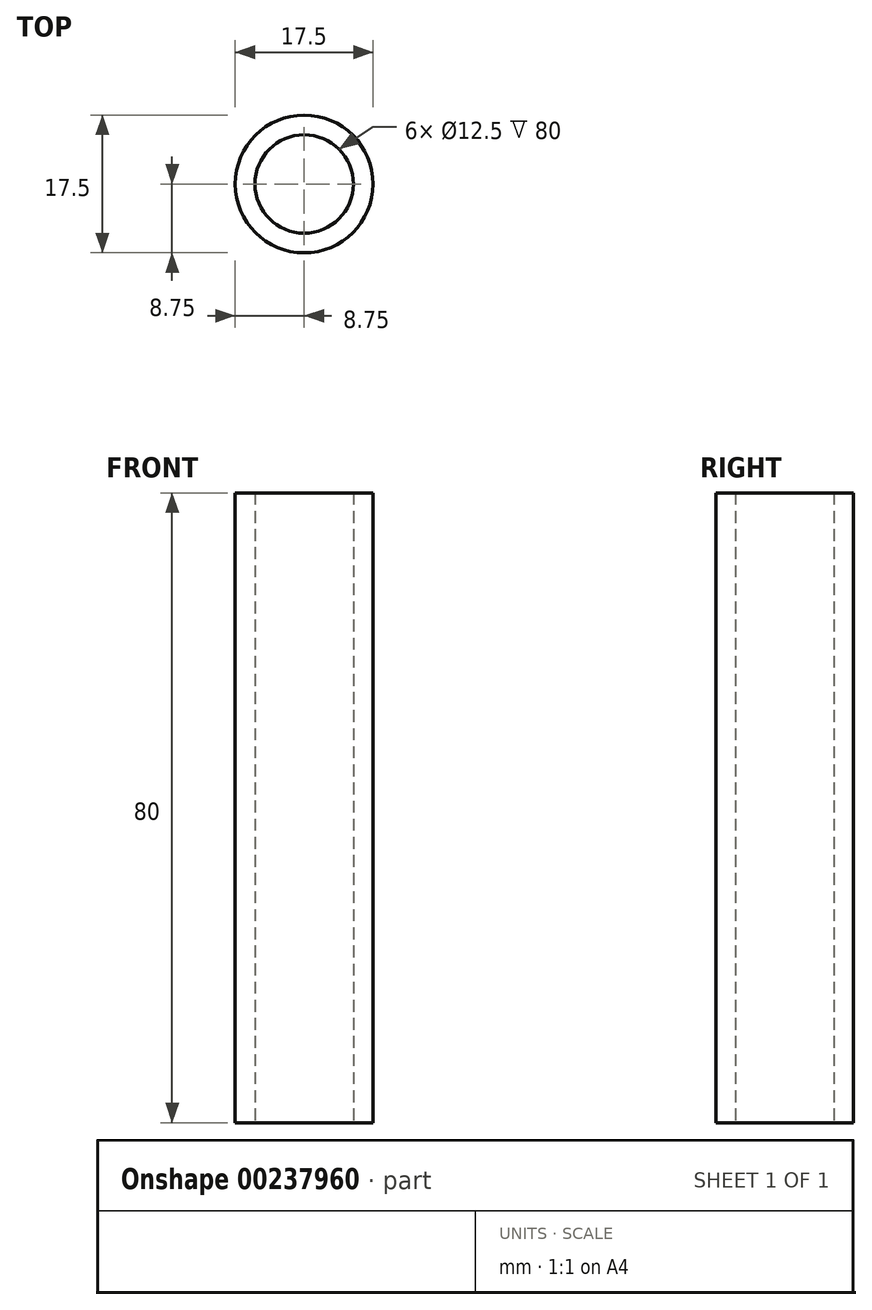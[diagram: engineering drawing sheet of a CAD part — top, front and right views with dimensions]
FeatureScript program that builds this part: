
annotation { "Feature Type Name" : "Feature", "Feature Type Description" : "" }
export const myFeature = defineFeature(function(context is Context, id is Id, definition is map)
    precondition{}
    {
        {
            var Q0;
            Q0=qCreatedBy(makeId("Top.planeOp"),FACE);
            var sketch = newSketch(context, id + "F0", { "sketchPlane" : qUnion([Q0])});
            skCircle(sketch, "E0", {"center": v(0, 0) * mm, "radius": 6.25 * mm});
            skCircle(sketch, "E1", {"center": v(0, 0) * mm, "radius": 8.75 * mm});
            skSolve(sketch);
        }
        {
            var Q0;
            Q0=makeQuery(id+"F0.imprint","IMPRINT",FACE,{"disambiguationData":[TD([[makeQuery(id+"F0.imprint","IMPRINT",EDGE,{"derivedFrom":sQuery(id+"F0.wireOp",EDGE,"E0")}),-1.0]])]});
            extrude(context, id + "F1", {"entities" : qUnion([Q0]), "depth" : 80 * mm});
        }
    });
